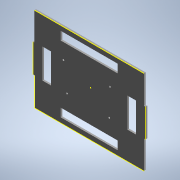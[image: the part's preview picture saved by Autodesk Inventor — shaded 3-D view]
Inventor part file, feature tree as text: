
AUTODESK INVENTOR PART (.ipt)
format: ipt  version: 2020 (Build 240168000, 168)  size: 172,032 bytes
history: native  units: mm (DEFAULTED — no unit token found)
features: sketch x14, extrude x9
ambient origin geometry x8: Origin, YZ Plane, XZ Plane, XY Plane, X Axis, Y Axis, Z Axis, Center Point
bodies: Solid1 (feature_tree)
feature tree (23):
  extrude  "Extrusion1"  Depth=3.0mm TaperAngle=0.0deg
  sketch  "Sketch2"  dims[d17=3.0mm d18=50.0mm]
  sketch  "Sketch3"  dims[d19=3.0mm d20=0.0mm d21=50.0mm]
  extrude  "Extrusion2"  Depth=50.0mm
  extrude  "Extrusion3"  Depth=50.0mm
  extrude  "Extrusion4"  Depth=3.0mm TaperAngle=0.0deg
  extrude  "Extrusion5"  Depth=3.0mm
  extrude  "Extrusion6"  Depth=15.0mm
  sketch  "Sketch9"  dims[d120=3.0mm d121=0.0mm]
  extrude  "Extrusion7"  Depth=3.0mm TaperAngle=0.0deg
  sketch  "Sketch11"
  extrude  "Extrusion8"  Depth=3.0mm TaperAngle=0.0deg
  extrude  "Extrusion9"  [1 undecoded]
  sketch  "Sketch14"
  sketch  "Sketch1"  dims[d2=3.0mm d3=0.0mm d15=3.0mm d16=0.0mm]
  sketch  "Sketch4"  dims[d22=3.0mm d23=3.0mm d24=0.0mm]
  sketch  "Sketch5"  dims[d25=50.0mm d26=3.0mm]
  sketch  "Sketch6"  dims[d27=3.0mm d28=0.0mm d32=15.0mm]
  sketch  "Sketch7"  dims[d33=30.0mm d34=3.0mm d35=0.0mm]
  sketch  "Sketch8"  dims[d36=30.0mm d37=0.0mm d77=3.0mm d78=0.0mm]
  sketch  "Sketch10"
  sketch  "Sketch12"
  sketch  "Sketch13"
note: 1 required parameter value undecoded (feature->parameter linkage not recoverable at this tier; creation-order binding heuristic only, values carry confidence <= 0.55)
